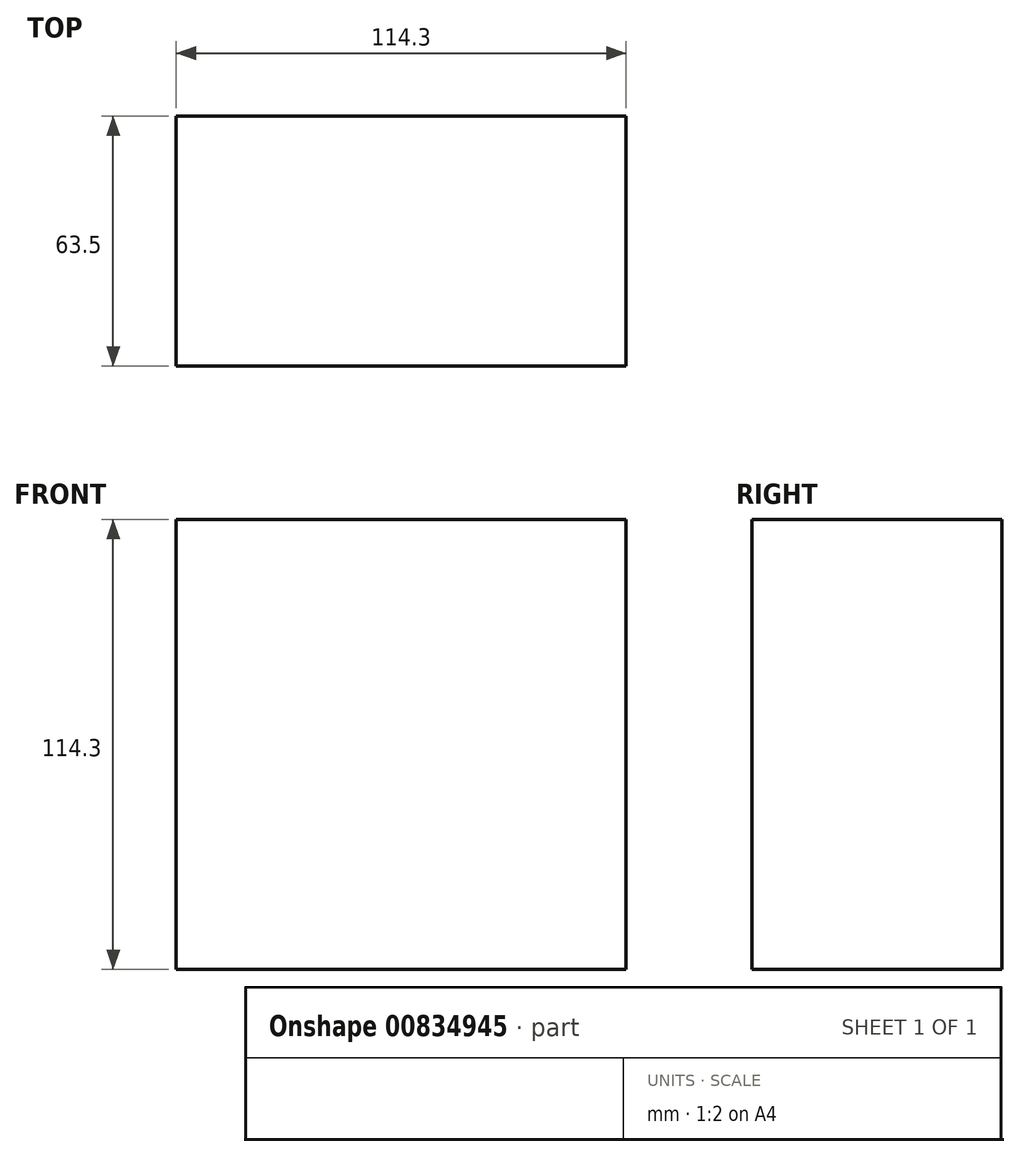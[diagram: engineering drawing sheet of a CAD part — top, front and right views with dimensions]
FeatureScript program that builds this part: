
annotation { "Feature Type Name" : "Feature", "Feature Type Description" : "" }
export const myFeature = defineFeature(function(context is Context, id is Id, definition is map)
    precondition{}
    {
        {
            var Q0;
            Q0=qCreatedBy(makeId("Top.planeOp"),FACE);
            var sketch = newSketch(context, id + "F0", { "sketchPlane" : qUnion([Q0])});
            skLineSegment(sketch, "E0.bottom", {"start": v(0, 0) * mm, "end": v(114.3, 0) * mm});
            skLineSegment(sketch, "E0.top", {"start": v(0, 63.5) * mm, "end": v(114.3, 63.5) * mm});
            skLineSegment(sketch, "E0.left", {"start": v(0, 0) * mm, "end": v(0, 63.5) * mm});
            skLineSegment(sketch, "E0.right", {"start": v(114.3, 0) * mm, "end": v(114.3, 63.5) * mm});
            skSolve(sketch);
        }
        {
            var Q0;
            Q0=qSketchRegion(id+"F0",true);
            extrude(context, id + "F1", {"entities" : qUnion([Q0]), "depth" : 114.3 * mm, "offsetDistance" : 25.4 * mm});
        }
    });
